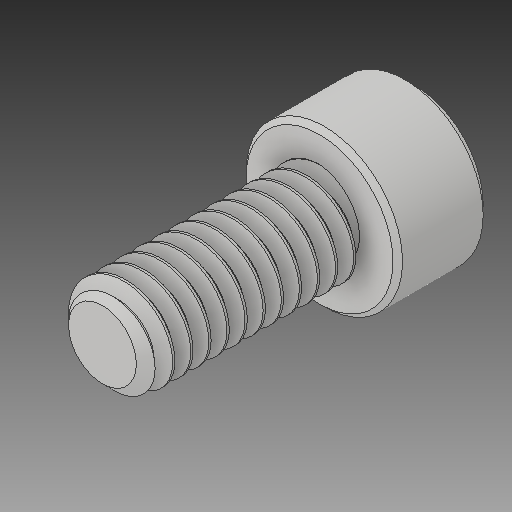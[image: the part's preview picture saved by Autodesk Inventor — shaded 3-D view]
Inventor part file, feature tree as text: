
AUTODESK INVENTOR PART (.ipt)
format: ipt  version: 2018 (Build 220112000, 112)  size: 599,040 bytes
history: native  units: in
note: dims shown in document units (in); Inventor stores cm internally (conversion verified against a paired STEP export)
features: chamfer x1
ambient origin geometry x8: Origin, YZ Plane, XZ Plane, XY Plane, X Axis, Y Axis, Z Axis, Center Point
bodies: Solid1 (feature_tree)
feature tree (1):
  chamfer  "Chamfer2"  [1 undecoded]
note: 1 required parameter value undecoded (feature->parameter linkage not recoverable at this tier; creation-order binding heuristic only, values carry confidence <= 0.55)
